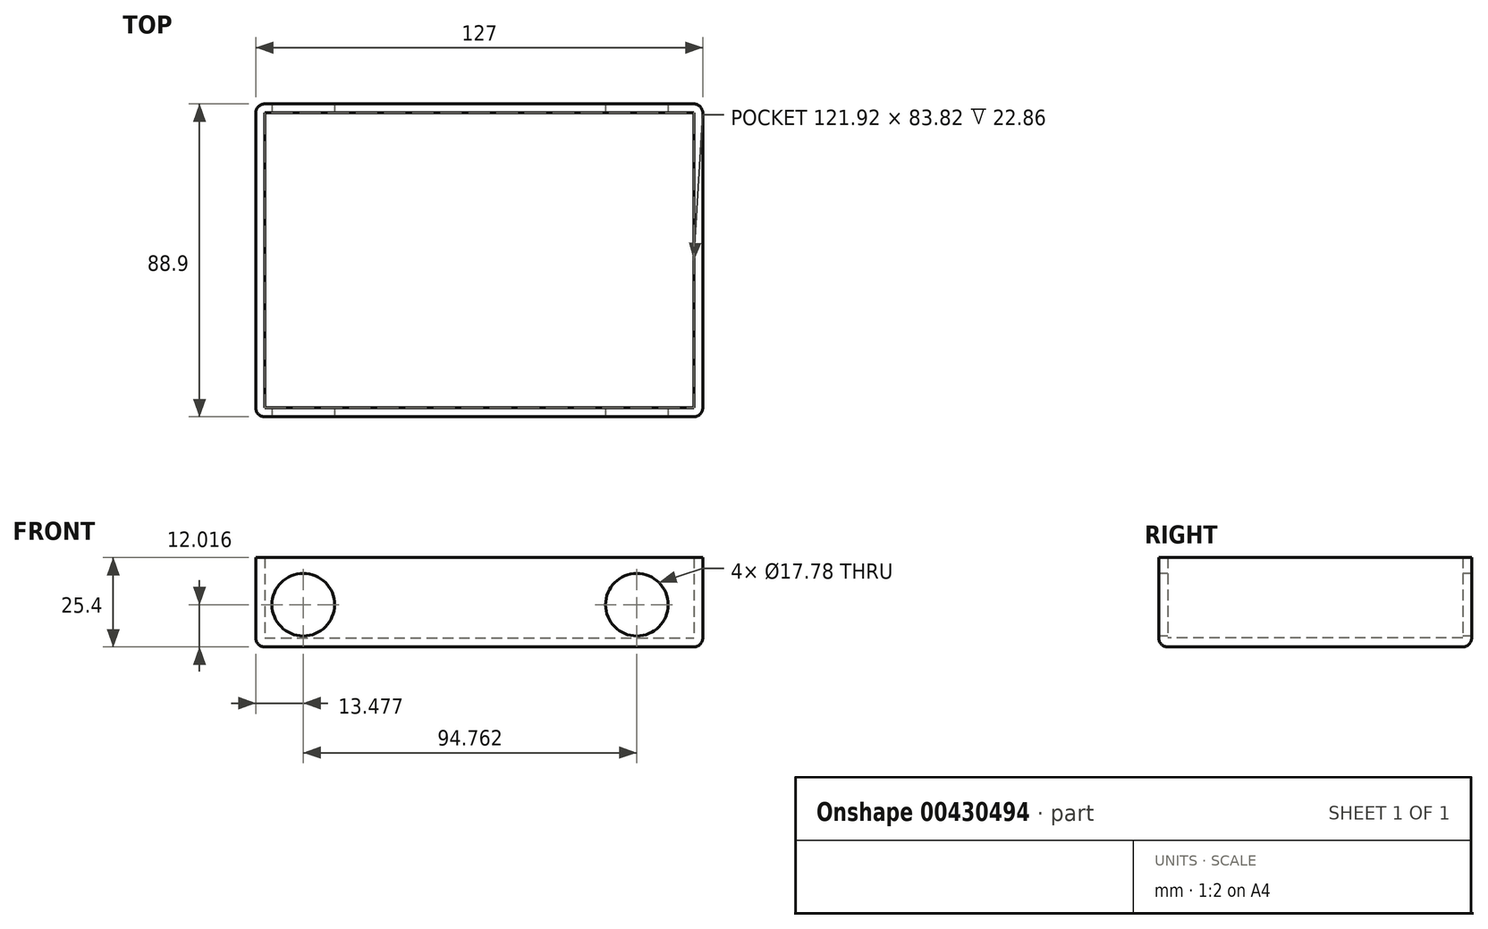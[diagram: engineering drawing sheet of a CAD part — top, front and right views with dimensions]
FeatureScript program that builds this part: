
annotation { "Feature Type Name" : "Feature", "Feature Type Description" : "" }
export const myFeature = defineFeature(function(context is Context, id is Id, definition is map)
    precondition{}
    {
        {
            var Q0;
            Q0=qCreatedBy(makeId("Top.planeOp"),FACE);
            var sketch = newSketch(context, id + "F0", { "sketchPlane" : qUnion([Q0])});
            skLineSegment(sketch, "E0.bottom", {"start": v(-60.76, 48.1) * mm, "end": v(66.24, 48.1) * mm});
            skLineSegment(sketch, "E0.top", {"start": v(-60.76, -40.8) * mm, "end": v(66.24, -40.8) * mm});
            skLineSegment(sketch, "E0.left", {"start": v(-60.76, 48.1) * mm, "end": v(-60.76, -40.8) * mm});
            skLineSegment(sketch, "E0.right", {"start": v(66.24, 48.1) * mm, "end": v(66.24, -40.8) * mm});
            skSolve(sketch);
        }
        {
            var Q0;
            Q0=makeQuery(id+"F0.imprint","IMPRINT",FACE,{"disambiguationData":[TD([[makeQuery(id+"F0.imprint","IMPRINT",EDGE,{"derivedFrom":sQuery(id+"F0.wireOp",EDGE,"E0.bottom")}),-1.0]])]});
            extrude(context, id + "F1", {"entities" : qUnion([Q0]), "depth" : 25.4 * mm});
        }
        {
            var Q0;
            Q0=makeQuery(id+"F1.opExtrude","CAP_FACE",FACE,{"disambiguationData":[OSD([sQuery(id+"F0.wireOp",EDGE,"E0.bottom"),sQuery(id+"F0.wireOp",EDGE,"E0.top"),sQuery(id+"F0.wireOp",EDGE,"E0.left"),sQuery(id+"F0.wireOp",EDGE,"E0.right")])],"isStart":false});
            shell(context, id + "F2", {"entities" : qUnion([Q0]), "thickness" : 2.54 * mm});
        }
        {
            var Q0;
            Q0=makeQuery(id+"F1.opExtrude","SWEPT_FACE",FACE,{"disambiguationData":[OSD([sQuery(id+"F0.wireOp",EDGE,"E0.top")])]});
            var sketch = newSketch(context, id + "F3", { "sketchPlane" : qUnion([Q0])});
            skCircle(sketch, "E1", {"center": v(-47.28, 12.02) * mm, "radius": 8.9 * mm});
            skCircle(sketch, "E2", {"center": v(47.48, 12.02) * mm, "radius": 8.9 * mm});
            skSolve(sketch);
        }
        {
            var Q0;
            Q0 = qSketchRegion(id + "F3", true);
            extrude(context, id + "F4", {"entities" : qUnion([Q0]), "operationType" : NewBodyOperationType.REMOVE, "oppositeDirection" : true, "depth" : 1270 * mm});
        }
        {
            var Q0;
            Q0=makeQuery(id+"F1.opExtrude","CAP_EDGE",EDGE,{"disambiguationData":[OSD([sQuery(id+"F0.wireOp",EDGE,"E0.right")])],"isStart":true});
            fillet(context, id + "F5", {"entities" : qUnion([Q0]), "radius" : 2.54 * mm, "tangentPropagation" : true, "allowEdgeOverflow" : false});
        }
        {
            var Q0;
            Q0=makeQuery(id+"F1.opExtrude","CAP_EDGE",EDGE,{"disambiguationData":[OSD([sQuery(id+"F0.wireOp",EDGE,"E0.top")])],"isStart":true});
            var Q1;
            Q1=makeQuery(id+"F1.opExtrude","SWEPT_EDGE",EDGE,{"disambiguationData":[OSD([sQuery(id+"F0.wireOp",EDGE,"E0.top"),sQuery(id+"F0.wireOp",EDGE,"E0.right")])]});
            var Q2;
            Q2=makeQuery(id+"F1.opExtrude","SWEPT_EDGE",EDGE,{"disambiguationData":[OSD([sQuery(id+"F0.wireOp",EDGE,"E0.bottom"),sQuery(id+"F0.wireOp",EDGE,"E0.right")])]});
            var Q3;
            Q3=makeQuery(id+"F1.opExtrude","CAP_EDGE",EDGE,{"disambiguationData":[OSD([sQuery(id+"F0.wireOp",EDGE,"E0.bottom")])],"isStart":true});
            var Q4;
            Q4=makeQuery(id+"F1.opExtrude","CAP_EDGE",EDGE,{"disambiguationData":[OSD([sQuery(id+"F0.wireOp",EDGE,"E0.left")])],"isStart":true});
            var Q5;
            Q5=makeQuery(id+"F1.opExtrude","SWEPT_EDGE",EDGE,{"disambiguationData":[OSD([sQuery(id+"F0.wireOp",EDGE,"E0.bottom"),sQuery(id+"F0.wireOp",EDGE,"E0.left")])]});
            var Q6;
            Q6=makeQuery(id+"F1.opExtrude","SWEPT_EDGE",EDGE,{"disambiguationData":[OSD([sQuery(id+"F0.wireOp",EDGE,"E0.top"),sQuery(id+"F0.wireOp",EDGE,"E0.left")])]});
            fillet(context, id + "F6", {"entities" : qUnion([Q0, Q1, Q2, Q3, Q4, Q5, Q6]), "radius" : 2.54 * mm, "tangentPropagation" : true, "allowEdgeOverflow" : false});
        }
    });
